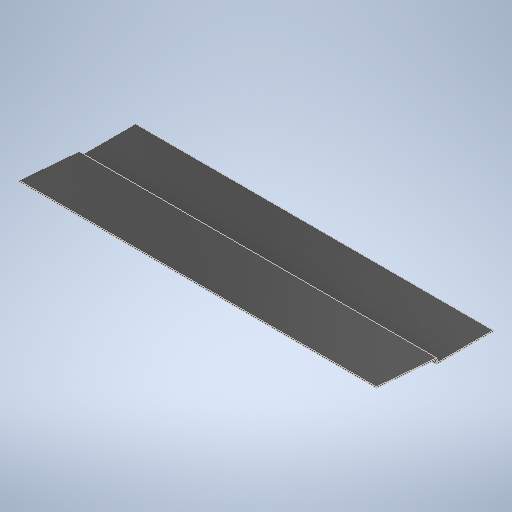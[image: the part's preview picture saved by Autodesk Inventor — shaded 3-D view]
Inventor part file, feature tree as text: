
AUTODESK INVENTOR PART (.ipt)
format: ipt  version: 2025.1 (Build 291241020, 241B)  size: 272,384 bytes
history: native  units: in
note: dims shown in document units (in); Inventor stores cm internally (conversion verified against a paired STEP export)
features: extrude x1, sketch x1
ambient origin geometry x8: Origin, YZ Plane, XZ Plane, XY Plane, X Axis, Y Axis, Z Axis, Center Point
bodies: Body1 (feature_tree)
feature tree (2):
  extrude  "Extrusion3"  Depth=0.125in
  sketch  "Sketch1"  dims[d0=23.408in d1=0.125in d2=0.265in d7=0.125in d8=0.237in d9=1.1431in d10=0.125in d11=0.7449in d12=0.125in d13=12.09in d18=0.125in d20=12.0907in d21=0.3425in d22=0.125in d23=0.125in d24=0.1549in d25=0.661in d28=0.125in d29=0.1254in d30=0.125in d32=0.125in d33=0.125in d34=5.625in d35=6.6451in d36=0.4476in d37=0.0449in d38=6.112in d39=39.375in d40=0.0in]
